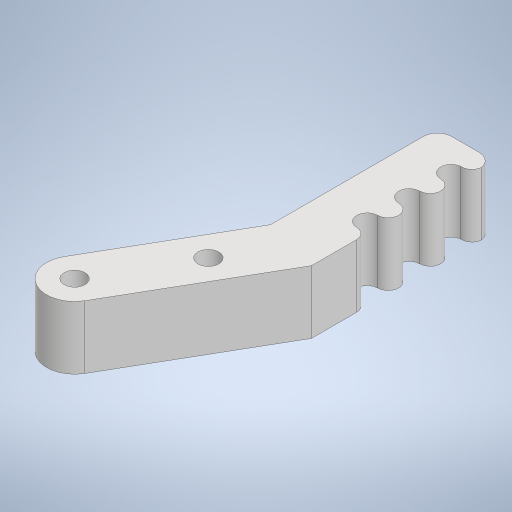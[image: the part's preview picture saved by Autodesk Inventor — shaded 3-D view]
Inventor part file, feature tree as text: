
AUTODESK INVENTOR PART (.ipt)
format: ipt  version: 2023 (Build 270158000, 158)  size: 274,432 bytes
history: native  units: mm
features: extrude x2, sketch x2, other x1
ambient origin geometry x8: Origin, YZ Plane, XZ Plane, XY Plane, X Axis, Y Axis, Z Axis, Center Point
bodies: Body1 (feature_tree), Body2 (feature_tree), Body3 (feature_tree)
feature tree (5):
  other  "Sólido1"
  extrude  "Extrusión1"  Depth=26.0mm
  extrude  "Extrusión2"  TaperAngle=150.0deg  [1 undecoded]
  sketch  "Boceto1"  dims[d0=90.0deg d2=26.0mm]
  sketch  "Boceto2"  dims[d7=8.0mm d10=150.0deg d11=8.0mm d12=5.0mm d13=4.0mm d14=4.0mm d15=2.0mm d16=3.0mm d17=3.0mm d18=14.0mm d19=48.0mm d20=9.0mm d21=0.0mm d24=3.0mm d25=3.0mm d26=3.0mm d27=3.0mm d28=3.0mm d29=3.0mm d30=3.0mm d31=1.5mm d33=9.0mm d34=0.0mm]
note: 1 required parameter value undecoded (feature->parameter linkage not recoverable at this tier; creation-order binding heuristic only, values carry confidence <= 0.55)
